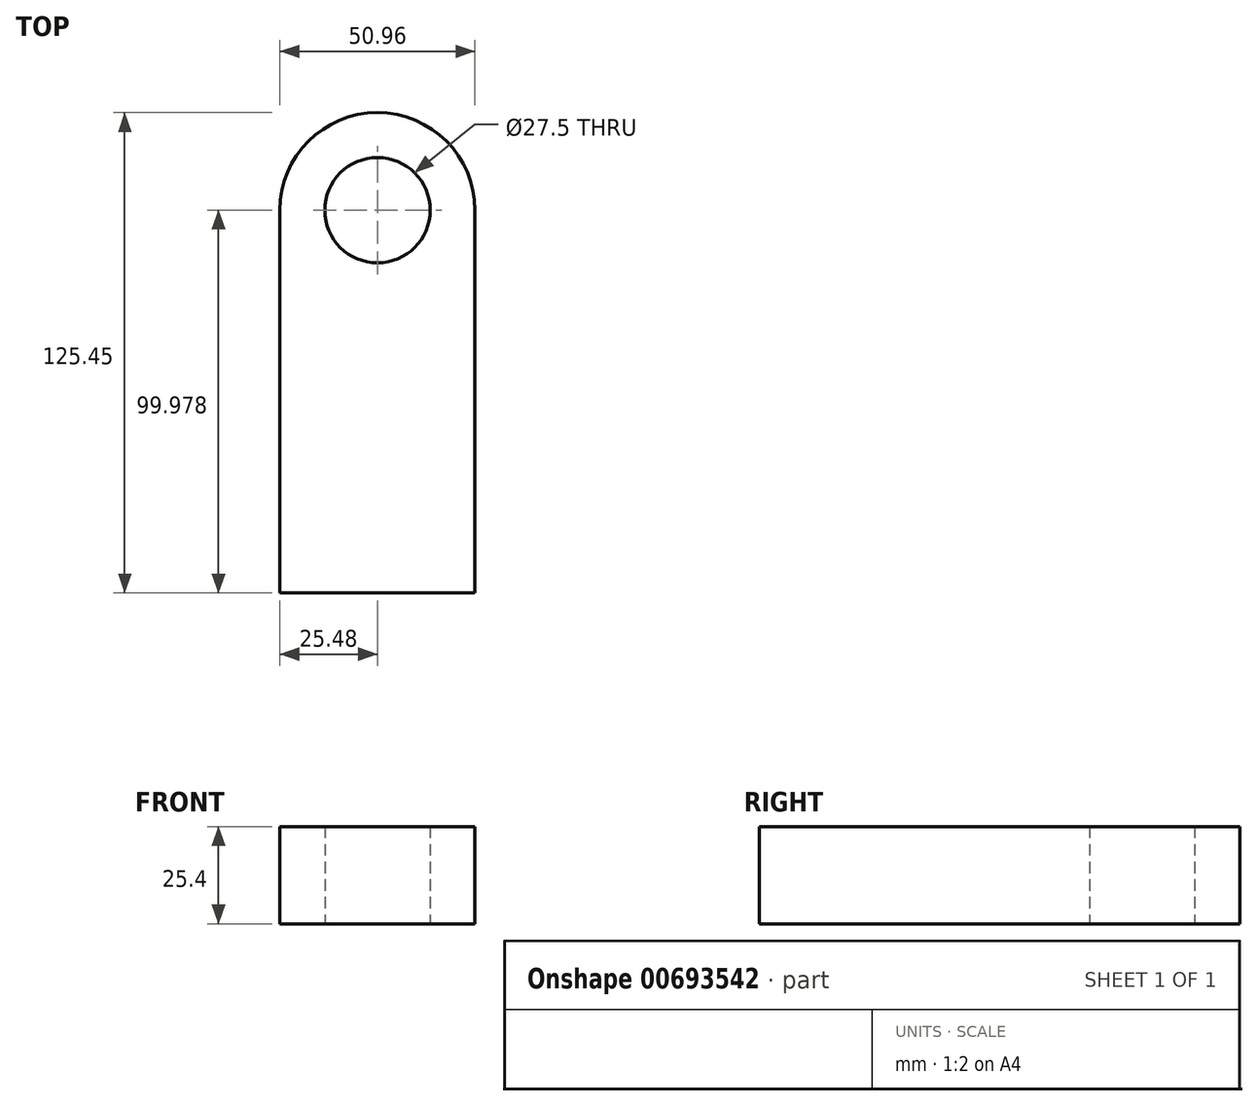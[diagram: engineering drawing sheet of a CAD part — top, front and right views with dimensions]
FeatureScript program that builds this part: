
annotation { "Feature Type Name" : "Feature", "Feature Type Description" : "" }
export const myFeature = defineFeature(function(context is Context, id is Id, definition is map)
    precondition{}
    {
        {
            var Q0;
            Q0=qCreatedBy(makeId("Top.planeOp"),FACE);
            var sketch = newSketch(context, id + "F0", { "sketchPlane" : qUnion([Q0])});
            skLineSegment(sketch, "E0.top", {"start": v(-25.48, -49.99) * mm, "end": v(25.48, -49.99) * mm});
            skLineSegment(sketch, "E0.left", {"start": v(-25.48, 49.99) * mm, "end": v(-25.48, -49.99) * mm});
            skLineSegment(sketch, "E0.right", {"start": v(25.48, 49.99) * mm, "end": v(25.48, -49.99) * mm});
            skPoint(sketch, "E0.middle", {"position": v(0, 0) * mm});
            skArc(sketch, "E1", {"start": v(25.48, 49.99) * mm, "mid": v(0, 75.46) * mm, "end": v(-25.48, 49.99) * mm});
            skCircle(sketch, "E2", {"center": v(0, 49.99) * mm, "radius": 13.75 * mm});
            skSolve(sketch);
        }
        {
            var Q0;
            Q0 = qSketchRegion(id + "F0", true);
            extrude(context, id + "F1", {"entities" : qUnion([Q0]), "depth" : 25.4 * mm, "offsetDistance" : 25.4 * mm});
        }
    });
